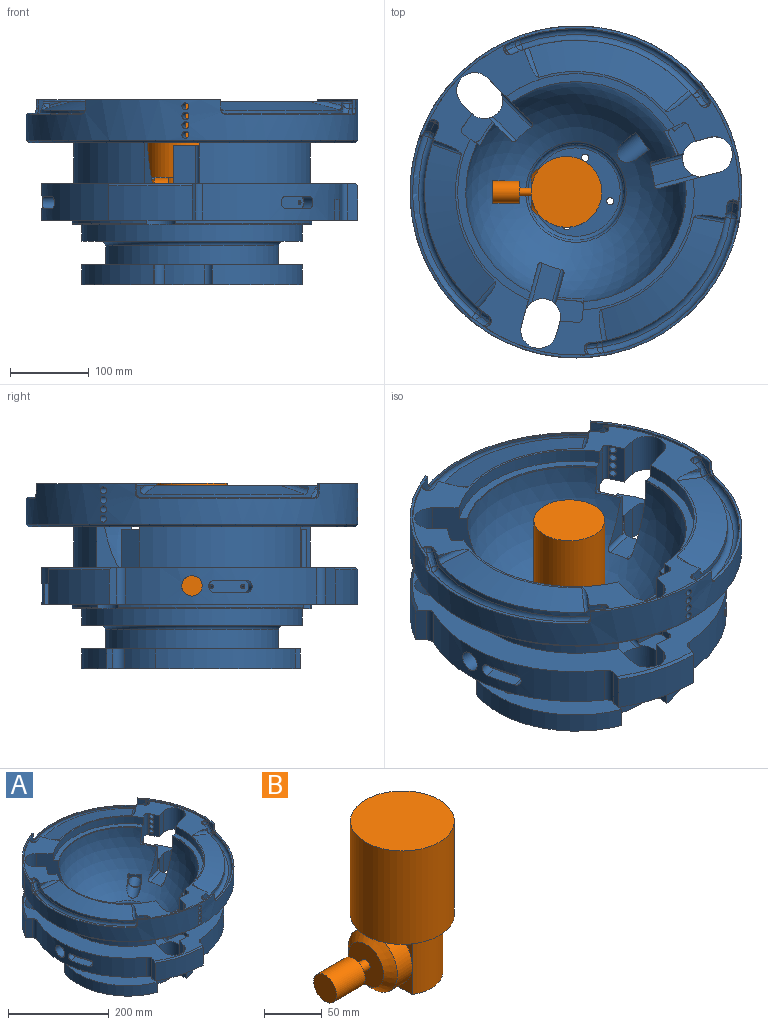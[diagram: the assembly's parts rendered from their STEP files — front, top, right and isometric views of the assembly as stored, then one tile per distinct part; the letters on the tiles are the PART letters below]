
ASSEMBLY  parts=2 mates=1
PART A: 307 faces, bbox 544.9x546.9x250.7 mm
  f0: cylinder r=2.1mm len=14.61mm, axis (-0.97,-0.26,0), area 184.7mm2, adj f1,f2
  f1: cone r=2.1mm half-angle=45deg, axis (-0.97,-0.26,0), area 10.4mm2, adj f0,f29
  f2: cone r=0mm half-angle=59deg, axis (-0.97,-0.26,0), area 16.2mm2, adj f0
  f3: cylinder r=2.1mm len=14.61mm, axis (-0.97,-0.26,0), area 184.7mm2, adj f4,f5
  f4: cone r=2.1mm half-angle=45deg, axis (-0.97,-0.26,0), area 10.4mm2, adj f3,f29
  f5: cone r=0mm half-angle=59deg, axis (-0.97,-0.26,0), area 16.2mm2, adj f3
  f6: cylinder r=2.1mm len=12.87mm, axis (0.71,-0.71,0), area 184.7mm2, adj f7,f8
  f7: cone r=2.1mm half-angle=45deg, axis (0.71,-0.71,0), area 10.4mm2, adj f6,f296
  f8: cone r=0mm half-angle=59deg, axis (0.71,-0.71,0), area 16.2mm2, adj f6
  f9: cylinder r=2.1mm len=12.87mm, axis (0.71,-0.71,0), area 184.7mm2, adj f10,f11
  f10: cone r=2.1mm half-angle=45deg, axis (0.71,-0.71,0), area 10.4mm2, adj f9,f296
  f11: cone r=0mm half-angle=59deg, axis (0.71,-0.71,0), area 16.2mm2, adj f9
  f12: cylinder r=4.5mm len=46.24mm, axis (0.09,1,0), area 1290mm2, adj f133,f243
  f13: cylinder r=4.5mm len=46.24mm, axis (0.09,1,0), area 1290mm2, adj f133,f243
  f14: cylinder r=4.5mm len=46.24mm, axis (0.09,1,0), area 1290mm2, adj f133,f243
  f15: cylinder r=4.5mm len=46.24mm, axis (0.09,1,0), area 1290mm2, adj f133,f243
  f16: plane 43.98x26.93mm, normal (0,0,-1), area 722.9mm2, adj f17,f19,f20,f286
  f17: cylinder r=8mm len=18.39mm, axis (0.26,0.97,0), area 424.6mm2, adj f16,f18,f20,f286
  f18: plane 43.98x26.93mm, normal (0,0,1), area 722.9mm2, adj f17,f19,f20,f286
  f19: cylinder r=8mm len=18.39mm, axis (0.26,0.97,0), area 424.6mm2, adj f16,f18,f20,f286
  f20: plane 55.06x16mm, normal (0.26,0.97,0), area 814.6mm2, adj f16,f17,f18,f19,f302,f305
  f21: cylinder r=4.5mm len=45.15mm, axis (-0.91,-0.42,0), area 1290mm2, adj f133,f251
  f22: cylinder r=4.5mm len=45.15mm, axis (-0.91,-0.42,0), area 1290mm2, adj f133,f251
  f23: cylinder r=4.5mm len=45.15mm, axis (-0.91,-0.42,0), area 1290mm2, adj f133,f251
  f24: cylinder r=4.5mm len=45.15mm, axis (-0.91,-0.42,0), area 1290mm2, adj f133,f251
  f25: plane 43.98x26.93mm, normal (0,0,-1), area 722.9mm2, adj f26,f28,f29,f291
  f26: cylinder r=8mm len=18.39mm, axis (-0.97,-0.26,0), area 424.6mm2, adj f25,f27,f29,f291
  f27: plane 43.98x26.93mm, normal (0,0,1), area 722.9mm2, adj f26,f28,f29,f291
  f28: cylinder r=8mm len=18.39mm, axis (-0.97,-0.26,0), area 424.6mm2, adj f25,f27,f29,f291
  f29: plane 55.06x16mm, normal (-0.97,-0.26,0), area 814.6mm2, adj f1,f4,f25,f26,f27,f28
  f30: cylinder r=190.75mm len=177.36mm, axis (0,0,-1), area 11210mm2, adj f36,f40,f41,f42,f67,f278,f279,f292
  f31: plane 30.27x25.75mm, normal (-0.97,-0.26,0), area 807mm2, adj f33,f36,f44,f286
  f32: plane 30.27x25.75mm, normal (0.97,0.26,0), area 807mm2, adj f33,f36,f46,f286
  f33: plane 41.19x32.46mm, normal (0,0,-1), area 811.8mm2, adj f31,f32,f43,f44,f45,f46,f286
  f34: cylinder r=210.75mm len=106.25mm, axis (0,0,1), area 4835.5mm2, adj f36,f37,f280,f284
  f35: cylinder r=210.75mm len=77.78mm, axis (0,0,1), area 4835.5mm2, adj f36,f38,f283,f290
  f36: plane 401.5x401.5mm, normal (0,0,-1), area 39749.9mm2, adj f30,f31,f32,f34,f35,f41,f42,f44
  f37: cone r=207.75mm half-angle=45deg, axis (0,0,-1), area 472.3mm2, adj f34,f67,f280,f284
  f38: cone r=207.75mm half-angle=45deg, axis (0,0,-1), area 472.3mm2, adj f35,f67,f283,f290
  f39: cylinder r=13mm len=84.25mm, axis (1,0,0), area 6881.7mm2, adj f144,f291
  f40: plane 41.19x32.46mm, normal (0,0,-1), area 811.8mm2, adj f30,f41,f42,f274,f275,f276,f277
  f41: plane 30.27x25.75mm, normal (0.26,0.97,0), area 807mm2, adj f30,f36,f40,f274
  f42: plane 30.27x25.75mm, normal (-0.26,-0.97,0), area 807mm2, adj f30,f36,f40,f276
  f43: cylinder r=6mm len=20.7mm, axis (0,0,-1), area 780.4mm2, adj f33,f67
  f44: cylinder r=6mm len=25.75mm, axis (0,0,-1), area 242.7mm2, adj f31,f33,f36,f45
  f45: plane 25.75x12.56mm, normal (-0.26,0.97,0), area 334.8mm2, adj f33,f36,f44,f46
  f46: cylinder r=6mm len=25.75mm, axis (0,0,-1), area 242.7mm2, adj f32,f33,f36,f45
  f47: cylinder r=210.75mm len=106.25mm, axis (0,0,1), area 4835.5mm2, adj f36,f139,f281,f289
  f48: cylinder r=7.01mm len=25mm, axis (0,0,-1), area 1101.1mm2, adj f63,f125
  f49: cylinder r=7.01mm len=25mm, axis (0,0,-1), area 1101.1mm2, adj f63,f125
  f50: cylinder r=140mm len=160.66mm, axis (0,0,1), area 5432.2mm2, adj f54,f57,f63,f125
  f51: plane 25x12.9mm, normal (1,-0.09,0), area 323.7mm2, adj f55,f62,f63,f125
  f52: cylinder r=115mm len=50.41mm, axis (0,0,-1), area 1275.4mm2, adj f53,f55,f63,f125
  f53: cylinder r=10mm len=25mm, axis (0,0,-1), area 448.2mm2, adj f52,f54,f63,f125
  f54: plane 25x12.9mm, normal (-1,0.09,0), area 323.7mm2, adj f50,f53,f63,f125
  f55: cylinder r=10mm len=25mm, axis (0,0,-1), area 448.2mm2, adj f51,f52,f63,f125
  f56: cylinder r=140mm len=195.38mm, axis (0,0,1), area 5432.2mm2, adj f60,f63,f125,f268
  f57: plane 25x11.73mm, normal (-0.42,0.91,0), area 323.7mm2, adj f50,f61,f63,f125
  f58: cylinder r=115mm len=45.86mm, axis (0,0,-1), area 1275.4mm2, adj f59,f61,f63,f125
  f59: cylinder r=10mm len=25mm, axis (0,0,-1), area 448.2mm2, adj f58,f60,f63,f125
  f60: plane 25x11.73mm, normal (0.42,-0.91,0), area 323.7mm2, adj f56,f59,f63,f125
  f61: cylinder r=10mm len=25mm, axis (0,0,-1), area 448.2mm2, adj f57,f58,f63,f125
  f62: cylinder r=140mm len=177.75mm, axis (0,0,1), area 5432.2mm2, adj f51,f63,f125,f272
  f63: plane 280x277.64mm, normal (0,0,1), area 17618.4mm2, adj f48,f49,f50,f51,f52,f53,f54,f55
  f64: cylinder r=22.93mm len=52.33mm, axis (0,0,1), area 2767.6mm2, adj f36,f67,f115,f118,f130,f131,f132,f145
  f65: cylinder r=22.93mm len=52.33mm, axis (0,0,1), area 2767.6mm2, adj f36,f67,f116,f117,f118,f130,f131,f150
  f66: cylinder r=22.93mm len=52.33mm, axis (0,0,1), area 2767.6mm2, adj f36,f67,f115,f116,f117,f130,f132,f155
  f67: plane 398.5x398.5mm, normal (0,0,1), area 40781.5mm2, adj f30,f37,f38,f43,f64,f65,f66,f102
  f68: plane 415.5x415.5mm, normal (0,0,-1), area 56548mm2, adj f69,f70,f71,f102,f103,f106,f140,f145
  f69: cylinder r=22.93mm len=51.85mm, axis (0,0,1), area 23.1mm2, adj f68,f84,f149,f243
  f70: cylinder r=22.93mm len=51.85mm, axis (0,0,1), area 23.1mm2, adj f68,f84,f151,f247
  f71: cylinder r=22.93mm len=51.85mm, axis (0,0,1), area 23.1mm2, adj f68,f84,f159,f251
  f72: plane 58.09x33.79mm, normal (0.26,-0.97,0), area 888.9mm2, adj f114,f166,f252,f255
  f73: plane 58.09x25.03mm, normal (0.71,0.71,0), area 888.9mm2, adj f114,f169,f248,f260
  f74: plane 58.09x33.79mm, normal (-0.97,0.26,0), area 888.9mm2, adj f114,f168,f244,f265
  f75: cylinder r=4.55mm len=60.1mm, axis (0,0,1), area 1718.2mm2, adj f137,f138
  f76: cylinder r=4.55mm len=60.1mm, axis (0,0,1), area 1718.2mm2, adj f137,f138
  f77: cylinder r=4.55mm len=60.1mm, axis (0,0,1), area 1718.2mm2, adj f137,f138
  f78: cone r=138.61mm half-angle=75deg, axis (0,0,-1), area 8140.1mm2, adj f84,f88,f89,f224
  f79: plane 12.58x10.55mm, normal (-0.77,0.64,0), area 36.1mm2, adj f84,f88,f224
  f80: plane 15.43x5.62mm, normal (-0.34,-0.94,0), area 36.1mm2, adj f84,f89,f224
  f81: cone r=138.61mm half-angle=75deg, axis (0,0,-1), area 8140.1mm2, adj f84,f90,f91,f205
  f82: plane 16.17x4.4mm, normal (-0.17,-0.98,0), area 36.1mm2, adj f84,f90,f205
  f83: plane 16.17x4.4mm, normal (0.98,0.17,0), area 36.1mm2, adj f84,f91,f205
  f84: plane 399.54x399.54mm, normal (0,0,1), area 18327.2mm2, adj f69,f70,f71,f78,f79,f80,f81,f82
  f85: cone r=138.61mm half-angle=75deg, axis (0,0,-1), area 8140.1mm2, adj f84,f92,f93,f186
  f86: plane 12.58x10.55mm, normal (-0.64,0.77,0), area 36.1mm2, adj f84,f93,f186
  f87: plane 15.43x5.62mm, normal (0.94,0.34,0), area 36.1mm2, adj f84,f92,f186
  f88: bspline ~109.4x92.16mm, area 271.4mm2, adj f78,f79,f84,f224
  f89: bspline ~165.06x65.44mm, area 271.4mm2, adj f78,f80,f84,f224
  f90: bspline ~136.78x42.3mm, area 271.4mm2, adj f81,f82,f84,f205
  f91: bspline ~173.42x52.26mm, area 271.4mm2, adj f81,f83,f84,f205
  f92: bspline ~130.1x52.71mm, area 271.4mm2, adj f84,f85,f87,f186
  f93: bspline ~137.91x116.08mm, area 271.4mm2, adj f84,f85,f86,f186
  f94: plane 172.06x51.8mm, normal (0,0,1), area 593.1mm2, adj f96,f101,f133,f163
  f95: cone r=138.61mm half-angle=75deg, axis (0,0,-1), area 819.6mm2, adj f133,f163,f174,f175
  f96: plane 12.29x2.49mm, normal (-0.77,0.64,0), area 38.5mm2, adj f94,f133,f163,f174
  f97: plane 12.29x3.05mm, normal (-0.34,-0.94,0), area 38.5mm2, adj f133,f163,f164,f175
  f98: plane 172.06x51.8mm, normal (0,0,1), area 593.1mm2, adj f100,f133,f163,f172
  f99: cone r=138.61mm half-angle=75deg, axis (0,0,-1), area 819.6mm2, adj f133,f163,f176,f177
  f100: plane 12.29x3.2mm, normal (-0.17,-0.98,0), area 38.5mm2, adj f98,f133,f163,f176
  f101: plane 12.29x3.2mm, normal (0.98,0.17,0), area 38.5mm2, adj f94,f133,f163,f177
  f102: cylinder r=150.25mm len=214.11mm, axis (0,0,1), area 12622.8mm2, adj f67,f68,f152,f250
  f103: cylinder r=150.25mm len=204.59mm, axis (0,0,1), area 12622.8mm2, adj f67,f68,f145,f246
  f104: cylinder r=150.25mm len=214.11mm, axis (0,0,1), area 4158.9mm2, adj f84,f109,f152,f250
  f105: cylinder r=150.25mm len=204.59mm, axis (0,0,1), area 4158.9mm2, adj f84,f110,f145,f246
  f106: cylinder r=150.25mm len=166.26mm, axis (0,0,1), area 12622.8mm2, adj f67,f68,f155,f242
  f107: cylinder r=150.25mm len=166.26mm, axis (0,0,1), area 4158.9mm2, adj f84,f108,f155,f242
  f108: plane 166.26x141.14mm, normal (0,0,1), area 2392mm2, adj f107,f111,f155,f242
  f109: plane 214.11x71.75mm, normal (0,0,1), area 2392mm2, adj f104,f112,f152,f250
  f110: plane 204.59x92.36mm, normal (0,0,1), area 2392mm2, adj f105,f113,f145,f246
  f111: cylinder r=140mm len=153.24mm, axis (0,0,1), area 447mm2, adj f108,f114,f155,f242
  f112: cylinder r=140mm len=197.37mm, axis (0,0,1), area 447mm2, adj f109,f114,f152,f250
  f113: cylinder r=140mm len=188.62mm, axis (0,0,1), area 447mm2, adj f110,f114,f145,f246
  f114: sphere r=140mm, area 91427.1mm2, adj f72,f73,f74,f111,f112,f113,f120,f121
  f115: cone r=152.35mm half-angle=15deg, axis (0,0,1), area 581.4mm2, adj f64,f66,f130,f132
  f116: cone r=152.35mm half-angle=15deg, axis (0,0,1), area 581.4mm2, adj f65,f66,f117,f130
  f117: cylinder r=152.35mm len=234.56mm, axis (0,0,1), area 1088.9mm2, adj f36,f65,f66,f116
  f118: cylinder r=152.35mm len=234.56mm, axis (0,0,1), area 1088.9mm2, adj f36,f64,f65,f131
  f119: cylinder r=13mm len=47.36mm, axis (-0.79,-0.61,0), area 3246.8mm2, adj f123,f180
  f120: plane 18.43x14.91mm, normal (0.61,-0.79,0), area 155.4mm2, adj f114,f121,f123
  f121: cylinder r=14mm len=46.85mm, axis (-0.79,-0.61,0), area 1330.4mm2, adj f114,f120,f122,f123
  f122: plane 18.43x14.91mm, normal (-0.61,0.79,0), area 155.4mm2, adj f114,f121,f123
  f123: plane 34.9x25.05mm, normal (-0.79,-0.61,0), area 262.4mm2, adj f114,f119,f120,f121,f122
  f124: cylinder r=105.88mm len=211.75mm, axis (0,0,1), area 7783.2mm2, adj f125,f138
  f125: plane 280x277.64mm, normal (0,0,-1), area 20416mm2, adj f48,f49,f50,f51,f52,f53,f54,f55
  f126: cylinder r=110mm len=220mm, axis (0,0,1), area 16587.6mm2, adj f63,f127
  f127: torus R=116mm, axis (0,0,1), area 6643mm2, adj f126,f128
  f128: plane 280x280mm, normal (0,0,-1), area 19301.9mm2, adj f127,f129
  f129: cylinder r=140mm len=280mm, axis (0,0,1), area 18406.6mm2, adj f128,f130
  f130: plane 303.64x303.64mm, normal (0,0,-1), area 9997.3mm2, adj f64,f65,f66,f115,f116,f129,f131
  f131: cone r=152.35mm half-angle=15deg, axis (0,0,1), area 581.4mm2, adj f64,f65,f118,f130
  f132: cylinder r=152.35mm len=173.13mm, axis (0,0,1), area 1088.9mm2, adj f36,f64,f66,f115
  f133: cylinder r=210.75mm len=421.5mm, axis (0,0,1), area 53750.8mm2, adj f12,f13,f14,f15,f21,f22,f23,f24
  f134: torus R=66.12mm, axis (0,0,1), area 2139.6mm2, adj f114,f135
  f135: cylinder r=61.12mm len=122.25mm, axis (0,0,1), area 2709.7mm2, adj f134,f136
  f136: torus R=56.12mm, axis (0,0,1), area 2926.7mm2, adj f135,f137
  f137: plane 112.25x112.25mm, normal (0,0,1), area 7672.4mm2, adj f75,f76,f77,f136,f239,f240
  f138: plane 211.75x211.75mm, normal (0,0,-1), area 32992.1mm2, adj f75,f76,f77,f124,f239,f240
  f139: cone r=207.75mm half-angle=45deg, axis (0,0,-1), area 472.3mm2, adj f47,f67,f281,f289
  f140: cone r=210.75mm half-angle=45deg, axis (0,0,1), area 5578mm2, adj f68,f133
  f141: plane 18.7x18.43mm, normal (0,1,0), area 155.4mm2, adj f114,f142,f144
  f142: cylinder r=14mm len=37.57mm, axis (1,0,0), area 1330.4mm2, adj f114,f141,f143,f144
  f143: plane 18.7x18.43mm, normal (0,-1,0), area 155.4mm2, adj f114,f142,f144
  f144: plane 34.9x30.84mm, normal (1,0,0), area 262.4mm2, adj f39,f114,f141,f142,f143
  f145: plane 154.52x81.4mm, normal (0.97,-0.26,0), area 4733.6mm2, adj f36,f64,f67,f68,f84,f103,f105,f110
  f146: cylinder r=22.93mm len=46.45mm, axis (0,0,1), area 3345.4mm2, adj f36,f67,f145,f148
  f147: cylinder r=22.93mm len=51.85mm, axis (0,0,1), area 3734.3mm2, adj f68,f84,f145,f149
  f148: plane 46.45x17.39mm, normal (-0.97,0.26,0), area 836.1mm2, adj f36,f64,f67,f146
  f149: plane 51.85x17.39mm, normal (-0.97,0.26,0), area 933.3mm2, adj f68,f69,f84,f147
  f150: plane 46.45x12.73mm, normal (0.71,0.71,0), area 836.1mm2, adj f36,f65,f67,f153
  f151: plane 51.85x12.73mm, normal (0.71,0.71,0), area 933.3mm2, adj f68,f70,f84,f154
  f152: plane 154.52x60.75mm, normal (-0.71,-0.71,0), area 4733.6mm2, adj f36,f65,f67,f68,f84,f102,f104,f109
  f153: cylinder r=22.93mm len=46.45mm, axis (0,0,1), area 3345.4mm2, adj f36,f67,f150,f152
  f154: cylinder r=22.93mm len=51.85mm, axis (0,0,1), area 3734.3mm2, adj f68,f84,f151,f152
  f155: plane 154.52x81.4mm, normal (-0.26,0.97,0), area 4733.6mm2, adj f36,f66,f67,f68,f84,f106,f107,f108
  f156: cylinder r=22.93mm len=46.45mm, axis (0,0,1), area 3345.4mm2, adj f36,f67,f155,f158
  f157: cylinder r=22.93mm len=51.85mm, axis (0,0,1), area 3734.3mm2, adj f68,f84,f155,f159
  f158: plane 46.45x17.39mm, normal (0.26,-0.97,0), area 836.1mm2, adj f36,f66,f67,f156
  f159: plane 51.85x17.39mm, normal (0.26,-0.97,0), area 933.3mm2, adj f68,f71,f84,f157
  f160: plane 54.65x35.47mm, normal (0,0,1), area 1084.7mm2, adj f66,f114,f165,f166
  f161: plane 52.95x48.6mm, normal (0,0,1), area 1084.7mm2, adj f65,f114,f169,f170
  f162: plane 49.5x37.06mm, normal (0,0,1), area 1084.7mm2, adj f64,f114,f167,f168
  f163: cylinder r=207.5mm len=415mm, axis (0,0,-1), area 4947.1mm2, adj f84,f94,f95,f96,f97,f98,f99,f100
  f164: plane 127.07x127.07mm, normal (0,0,1), area 593.1mm2, adj f97,f133,f163,f173
  f165: cylinder r=5mm len=64.6mm, axis (0.97,0.26,0), area 444mm2, adj f66,f114,f155,f160
  f166: cylinder r=5mm len=44.26mm, axis (-0.97,-0.26,0), area 314.7mm2, adj f66,f72,f114,f160,f254,f255
  f167: cylinder r=5mm len=64.6mm, axis (-0.26,-0.97,0), area 444mm2, adj f64,f114,f145,f162
  f168: cylinder r=5mm len=44.26mm, axis (0.26,0.97,0), area 314.7mm2, adj f64,f74,f114,f162,f264,f265
  f169: cylinder r=5mm len=34.99mm, axis (0.71,-0.71,0), area 314.7mm2, adj f65,f73,f114,f161,f259,f260
  f170: cylinder r=5mm len=49.88mm, axis (-0.71,0.71,0), area 444mm2, adj f65,f114,f152,f161
  f171: cone r=138.61mm half-angle=75deg, axis (0,0,-1), area 819.6mm2, adj f133,f163,f178,f179
  f172: plane 12.29x2.49mm, normal (-0.64,0.77,0), area 38.5mm2, adj f98,f133,f163,f179
  f173: plane 12.29x3.05mm, normal (0.94,0.34,0), area 38.5mm2, adj f133,f163,f164,f178
  f174: bspline ~74.28x62.69mm, area 31.6mm2, adj f95,f96,f133,f163
  f175: bspline ~122.16x49.84mm, area 31.6mm2, adj f95,f97,f133,f163
  f176: bspline ~91.62x30.02mm, area 31.6mm2, adj f99,f100,f133,f163
  f177: bspline ~128.46x40.04mm, area 31.6mm2, adj f99,f101,f133,f163
  f178: bspline ~87x37.05mm, area 31.6mm2, adj f133,f163,f171,f173
  f179: bspline ~102.94x86.74mm, area 31.6mm2, adj f133,f163,f171,f172
  f180: plane 40x31.73mm, normal (0.79,0.61,0), area 712.8mm2, adj f119,f181,f250,f254
  f181: cylinder r=20mm len=61.91mm, axis (0.79,0.61,0), area 5531.6mm2, adj f180,f250,f254,f257,f285,f286
  f182: cylinder r=7.6mm len=10.05mm, axis (0,0,1), area 17.5mm2, adj f84,f185,f186,f188
  f183: cylinder r=7.6mm len=10.53mm, axis (0,0,1), area 17.5mm2, adj f84,f163,f184,f198
  f184: cylinder r=7.6mm len=10.5mm, axis (0,0,1), area 17.5mm2, adj f84,f183,f186,f200
  f185: cylinder r=7.6mm len=10mm, axis (0,0,1), area 17.5mm2, adj f84,f163,f182,f187
  f186: cylinder r=192.5mm len=238.4mm, axis (0,0,1), area 1972.5mm2, adj f84,f85,f86,f87,f92,f93,f182,f184
  f187: bspline ~10.49x8.97mm, area 67.3mm2, adj f163,f185,f188,f189,f190
  f188: bspline ~10.88x8.95mm, area 66.9mm2, adj f182,f186,f187,f190
  f189: bspline ~40.78x38.51mm, area 233.2mm2, adj f163,f187,f190,f192,f193
  f190: bspline ~40.19x39.53mm, area 219.9mm2, adj f186,f187,f188,f189,f193
  f191: torus R=199.9mm, axis (0,0,1), area 2987.3mm2, adj f163,f192,f194,f195
  f192: bspline ~11.37x10.69mm, area 69.2mm2, adj f163,f189,f191,f193,f195
  f193: bspline ~10.85x10.22mm, area 65mm2, adj f186,f189,f190,f192,f195
  f194: bspline ~12.04x11.72mm, area 69.2mm2, adj f163,f191,f195,f196,f197
  f195: torus R=200.1mm, axis (0,0,1), area 2848.3mm2, adj f186,f191,f192,f193,f194,f197
  f196: bspline ~40.78x36.81mm, area 233.2mm2, adj f163,f194,f197,f198,f199
  f197: bspline ~11.52x11.18mm, area 65mm2, adj f186,f194,f195,f196,f199
  f198: bspline ~11.36x8.97mm, area 67.3mm2, adj f163,f183,f196,f199,f200
  f199: bspline ~40.19x31.52mm, area 219.9mm2, adj f186,f196,f197,f198,f200
  f200: bspline ~11.09x8.95mm, area 66.9mm2, adj f184,f186,f198,f199
  f201: cylinder r=7.6mm len=8.24mm, axis (0,0,1), area 17.5mm2, adj f84,f163,f202,f206
  f202: cylinder r=7.6mm len=8.15mm, axis (0,0,1), area 17.5mm2, adj f84,f201,f205,f207
  f203: cylinder r=7.6mm len=8.24mm, axis (0,0,1), area 17.5mm2, adj f84,f163,f204,f217
  f204: cylinder r=7.6mm len=8.15mm, axis (0,0,1), area 17.5mm2, adj f84,f203,f205,f219
  f205: cylinder r=192.5mm len=174.52mm, axis (0,0,1), area 1972.5mm2, adj f81,f82,f83,f84,f90,f91,f202,f204
  f206: bspline ~9.18x8.97mm, area 67.3mm2, adj f163,f201,f207,f208,f209
  f207: bspline ~8.95x8.43mm, area 66.9mm2, adj f202,f205,f206,f209
  f208: bspline ~41.61x40.78mm, area 233.2mm2, adj f163,f206,f209,f211,f212
  f209: bspline ~40.19x38.59mm, area 219.9mm2, adj f205,f206,f207,f208,f212
  f210: torus R=199.9mm, axis (0,0,1), area 2987.3mm2, adj f163,f211,f213,f214
  f211: bspline ~10.17x8.93mm, area 69.2mm2, adj f163,f208,f210,f212,f214
  f212: bspline ~9.24x8.46mm, area 65mm2, adj f205,f208,f209,f211,f214
  f213: bspline ~10.17x8.93mm, area 69.2mm2, adj f163,f210,f214,f215,f216
  f214: torus R=200.1mm, axis (0,0,1), area 2848.3mm2, adj f205,f210,f211,f212,f213,f216
  f215: bspline ~41.61x40.78mm, area 233.2mm2, adj f163,f213,f216,f217,f218
  f216: bspline ~9.74x8.53mm, area 65mm2, adj f205,f213,f214,f215,f218
  f217: bspline ~9.18x8.97mm, area 67.3mm2, adj f163,f203,f215,f218,f219
  f218: bspline ~40.19x38.59mm, area 219.9mm2, adj f205,f215,f216,f217,f219
  f219: bspline ~8.95x8.43mm, area 66.9mm2, adj f204,f205,f217,f218
  f220: cylinder r=7.6mm len=10.53mm, axis (0,0,1), area 17.5mm2, adj f84,f163,f221,f225
  f221: cylinder r=7.6mm len=10.5mm, axis (0,0,1), area 17.5mm2, adj f84,f220,f224,f226
  f222: cylinder r=7.6mm len=10.05mm, axis (0,0,1), area 17.5mm2, adj f84,f223,f224,f238
  f223: cylinder r=7.6mm len=10mm, axis (0,0,1), area 17.5mm2, adj f84,f163,f222,f236
  f224: cylinder r=192.5mm len=238.4mm, axis (0,0,1), area 1972.5mm2, adj f78,f79,f80,f84,f88,f89,f221,f222
  f225: bspline ~11.36x8.97mm, area 67.3mm2, adj f163,f220,f226,f227,f228
  f226: bspline ~11.09x8.95mm, area 66.9mm2, adj f221,f224,f225,f228
  f227: bspline ~40.78x36.81mm, area 233.2mm2, adj f163,f225,f228,f230,f231
  f228: bspline ~40.19x31.52mm, area 219.9mm2, adj f224,f225,f226,f227,f231
  f229: torus R=199.9mm, axis (0,0,1), area 2987.3mm2, adj f163,f230,f232,f233
  f230: bspline ~12.04x11.72mm, area 69.2mm2, adj f163,f227,f229,f231,f233
  f231: bspline ~11.52x11.18mm, area 65mm2, adj f224,f227,f228,f230,f233
  f232: bspline ~11.37x10.69mm, area 69.2mm2, adj f163,f229,f233,f234,f235
  f233: torus R=200.1mm, axis (0,0,1), area 2848.3mm2, adj f224,f229,f230,f231,f232,f235
  f234: bspline ~40.78x38.51mm, area 233.2mm2, adj f163,f232,f235,f236,f237
  f235: bspline ~10.06x9.88mm, area 65mm2, adj f224,f232,f233,f234,f237
  f236: bspline ~10.49x8.97mm, area 67.3mm2, adj f163,f223,f234,f237,f238
  f237: bspline ~40.19x39.53mm, area 219.9mm2, adj f224,f234,f235,f236,f238
  f238: bspline ~10.88x8.95mm, area 66.9mm2, adj f222,f224,f236,f237
  f239: cylinder r=25mm len=60.1mm, axis (0,0,1), area 9440.5mm2, adj f137,f138
  f240: cylinder r=4.55mm len=60.1mm, axis (0,0,1), area 1718.2mm2, adj f137,f138
  f241: cylinder r=6mm len=51.85mm, axis (0,0,1), area 488.7mm2, adj f68,f84,f242,f243
  f242: plane 114.19x25.85mm, normal (-1,0.09,0), area 1372.6mm2, adj f67,f68,f84,f106,f107,f108,f111,f114
  f243: plane 51.85x21.9mm, normal (0.09,1,0), area 885.1mm2, adj f12,f13,f14,f15,f68,f69,f84,f241
  f244: plane 34.46x11.97mm, normal (0,0,1), area 110.8mm2, adj f74,f114,f242,f265,f266
  f245: cylinder r=6mm len=51.85mm, axis (0,0,1), area 488.7mm2, adj f68,f84,f246,f247
  f246: plane 114.19x21.33mm, normal (0.57,0.82,0), area 1372.6mm2, adj f67,f68,f84,f103,f105,f110,f113,f114
  f247: plane 51.85x18mm, normal (0.82,-0.57,0), area 885.1mm2, adj f68,f70,f84,f245,f297,f298,f299,f300
  f248: plane 30.55x26.74mm, normal (0,0,1), area 110.8mm2, adj f73,f114,f246,f260,f261
  f249: cylinder r=6mm len=51.85mm, axis (0,0,1), area 488.7mm2, adj f68,f84,f250,f251
  f250: plane 114.24x23.6mm, normal (0.42,-0.91,0), area 1325.4mm2, adj f67,f68,f84,f102,f104,f109,f112,f114
  f251: plane 51.85x19.92mm, normal (-0.91,-0.42,0), area 885.1mm2, adj f21,f22,f23,f24,f68,f71,f84,f249
  f252: plane 34.34x18.45mm, normal (0,0,1), area 110.8mm2, adj f72,f114,f250,f255,f256
  f253: plane 19.92x10.05mm, normal (-0.91,-0.42,0), area 220.9mm2, adj f66,f67,f254,f257
  f254: plane 40.58x34.46mm, normal (0,0,1), area 767.9mm2, adj f66,f166,f180,f181,f250,f253,f255,f256
  f255: plane 58.83x25.9mm, normal (0.91,0.42,0), area 1658.6mm2, adj f72,f166,f252,f254,f256
  f256: cylinder r=6mm len=58.8mm, axis (0,0,1), area 554.2mm2, adj f250,f252,f254,f255
  f257: cylinder r=6mm len=10.05mm, axis (0,0,1), area 90mm2, adj f67,f181,f250,f253,f254
  f258: plane 18x12.61mm, normal (0.82,-0.57,0), area 220.9mm2, adj f65,f67,f259,f262
  f259: plane 39.7x36.14mm, normal (0,0,1), area 825.5mm2, adj f65,f169,f246,f258,f260,f261,f262
  f260: plane 58.83x23.41mm, normal (-0.82,0.57,0), area 1658.6mm2, adj f73,f169,f248,f259,f261
  f261: cylinder r=6mm len=58.8mm, axis (0,0,1), area 554.2mm2, adj f246,f248,f259,f260
  f262: cylinder r=6mm len=10.05mm, axis (0,0,1), area 94.7mm2, adj f67,f246,f258,f259
  f263: plane 21.9x10.05mm, normal (0.09,1,0), area 220.9mm2, adj f64,f67,f264,f267
  f264: plane 35.56x29.56mm, normal (0,0,1), area 825.5mm2, adj f64,f168,f242,f263,f265,f266,f267
  f265: plane 58.83x28.47mm, normal (-0.09,-1,0), area 1658.6mm2, adj f74,f168,f244,f264,f266
  f266: cylinder r=6mm len=58.8mm, axis (0,0,1), area 554.2mm2, adj f242,f244,f264,f265
  f267: cylinder r=6mm len=10.05mm, axis (0,0,1), area 94.7mm2, adj f67,f242,f263,f264
  f268: plane 25x10.61mm, normal (-0.57,-0.82,0), area 323.7mm2, adj f56,f63,f125,f269
  f269: cylinder r=10mm len=25mm, axis (0,0,-1), area 448.2mm2, adj f63,f125,f268,f270
  f270: cylinder r=115mm len=41.45mm, axis (0,0,-1), area 1275.4mm2, adj f63,f125,f269,f271
  f271: cylinder r=10mm len=25mm, axis (0,0,-1), area 448.2mm2, adj f63,f125,f270,f272
  f272: plane 25x10.61mm, normal (0.57,0.82,0), area 323.7mm2, adj f62,f63,f125,f271
  f273: cylinder r=7.01mm len=25mm, axis (0,0,-1), area 1101.1mm2, adj f63,f125
  f274: cylinder r=6mm len=25.75mm, axis (0,0,-1), area 242.7mm2, adj f36,f40,f41,f275
  f275: plane 25.75x12.56mm, normal (0.97,-0.26,0), area 334.8mm2, adj f36,f40,f274,f276
  f276: cylinder r=6mm len=25.75mm, axis (0,0,-1), area 242.7mm2, adj f36,f40,f42,f275
  f277: cylinder r=6mm len=20.7mm, axis (0,0,-1), area 780.4mm2, adj f40,f67
  f278: cylinder r=10mm len=46.45mm, axis (0,0,-1), area 576.5mm2, adj f30,f36,f67,f281
  f279: cylinder r=10mm len=46.45mm, axis (0,0,-1), area 576.5mm2, adj f30,f36,f67,f280
  f280: plane 46.46x13.06mm, normal (0.26,-0.97,0), area 622.9mm2, adj f34,f36,f37,f67,f279
  f281: plane 46.46x13.06mm, normal (0.97,-0.26,0), area 622.9mm2, adj f36,f47,f67,f139,f278
  f282: cylinder r=10mm len=46.45mm, axis (0,0,-1), area 576.5mm2, adj f36,f67,f283,f286
  f283: plane 46.46x9.56mm, normal (0.71,0.71,0), area 622.9mm2, adj f35,f36,f38,f67,f282
  f284: plane 46.46x13.06mm, normal (-0.26,0.97,0), area 622.9mm2, adj f34,f36,f37,f67,f285
  f285: cylinder r=10mm len=46.45mm, axis (0,0,-1), area 384.6mm2, adj f36,f67,f181,f284,f286
  f286: cylinder r=190.75mm len=242.28mm, axis (0,0,-1), area 10132.7mm2, adj f16,f17,f18,f19,f31,f32,f33,f36
  f287: cylinder r=10mm len=46.45mm, axis (0,0,-1), area 576.5mm2, adj f36,f67,f290,f291
  f288: cylinder r=10mm len=46.45mm, axis (0,0,-1), area 576.5mm2, adj f36,f67,f289,f291
  f289: plane 46.46x13.06mm, normal (-0.97,0.26,0), area 622.9mm2, adj f36,f47,f67,f139,f288
  f290: plane 46.46x9.56mm, normal (-0.71,-0.71,0), area 622.9mm2, adj f35,f36,f38,f67,f287
  f291: cylinder r=190.75mm len=242.28mm, axis (0,0,-1), area 11322mm2, adj f25,f26,f27,f28,f36,f39,f67,f287
  f292: plane 40.94x40.94mm, normal (0,0,-1), area 722.9mm2, adj f30,f293,f295,f296
  f293: cylinder r=8mm len=17.6mm, axis (0.71,-0.71,0), area 424.6mm2, adj f30,f292,f294,f296
  f294: plane 40.94x40.94mm, normal (0,0,1), area 722.9mm2, adj f30,f293,f295,f296
  f295: cylinder r=8mm len=17.6mm, axis (0.71,-0.71,0), area 424.6mm2, adj f30,f292,f294,f296
  f296: plane 40.31x40.31mm, normal (0.71,-0.71,0), area 814.6mm2, adj f7,f10,f292,f293,f294,f295
  f297: cylinder r=4.5mm len=42.54mm, axis (0.82,-0.57,0), area 1290mm2, adj f133,f247
  f298: cylinder r=4.5mm len=42.54mm, axis (0.82,-0.57,0), area 1290mm2, adj f133,f247
  f299: cylinder r=4.5mm len=42.54mm, axis (0.82,-0.57,0), area 1290mm2, adj f133,f247
  f300: cylinder r=4.5mm len=42.54mm, axis (0.82,-0.57,0), area 1290mm2, adj f133,f247
  f301: cylinder r=2.1mm len=14.61mm, axis (0.26,0.97,0), area 184.7mm2, adj f302,f303
  f302: cone r=2.1mm half-angle=45deg, axis (0.26,0.97,0), area 10.4mm2, adj f20,f301
  f303: cone r=0mm half-angle=59deg, axis (0.26,0.97,0), area 16.2mm2, adj f301
  f304: cylinder r=2.1mm len=14.61mm, axis (0.26,0.97,0), area 184.7mm2, adj f305,f306
  f305: cone r=2.1mm half-angle=45deg, axis (0.26,0.97,0), area 10.4mm2, adj f20,f304
  f306: cone r=0mm half-angle=59deg, axis (0.26,0.97,0), area 16.2mm2, adj f304
PART B: 15 faces, bbox 139.5x90x160 mm
  f0: cylinder r=35mm len=61mm, axis (0,0,-1), area 3351.7mm2, adj f1,f3,f4,f12
  f1: plane 61x60.03mm, normal (-1,0,0), area 834.6mm2, adj f0,f2,f4,f5,f12
  f2: cylinder r=35mm len=61mm, axis (0,0,-1), area 3351.7mm2, adj f1,f3,f4,f12
  f3: plane 61x36.06mm, normal (1,0,0), area 2199.4mm2, adj f0,f2,f4,f12
  f4: plane 70x48mm, normal (0,0,-1), area 3004.2mm2, adj f0,f1,f2,f3
  f5: cylinder r=30mm len=60mm, axis (1,0,0), area 3392.9mm2, adj f1,f7
  f6: plane 43x43mm, normal (-1,0,0), area 1373.7mm2, adj f7,f8
  f7: cone r=21.5mm half-angle=45deg, axis (1,0,0), area 1944.9mm2, adj f5,f6
  f8: cylinder r=5mm len=15mm, axis (-1,0,0), area 471.2mm2, adj f6,f9
  f9: plane 28x28mm, normal (1,0,0), area 537.2mm2, adj f8,f10
  f10: cylinder r=14mm len=35mm, axis (-1,0,0), area 3078.8mm2, adj f9,f11
  f11: plane 28x28mm, normal (-1,0,0), area 615.8mm2, adj f10
  f12: plane 90x90mm, normal (0,0,-1), area 3357.5mm2, adj f0,f1,f2,f3,f13
  f13: cylinder r=45mm len=99mm, axis (0,0,1), area 27991.6mm2, adj f12,f14
  f14: plane 90x90mm, normal (0,0,1), area 6361.7mm2, adj f13
PLACE A t=(-51.73,-62.21,-309.77)mm
PLACE B t=(-63.83,-62.21,-234.72)mm
MATE slider A.f39 <-> B.f8  axis (1,0,0) through (-139.33,-62.21,-204.72)mm
